# Revit family: NAU_Naughtone_Stng_Viv_4Leg1
name_source: partatom
category: Furniture
revit_build: Autodesk Revit 2018 (Build: 20170223_1515(x64)
units: mm (PartAtom-declared; Revit-internal decimal feet)

## family parameters
Always vertical = Yes
Cut with Voids When Loaded = No
OmniClass Number = 23.40.20.00
OmniClass Title = General Furniture and Specialties
Room Calculation Point = No
Shared = Yes
Work Plane-Based = No

## types (2) — shared parameters
Assembly Code = E2020200
AssetType = Movable
BIMObjectName = NAU_Naughtone_Seating_Viv_4Leg
Category = Pr_40_50_12 : Chairs, seats and benches
Color = Various
DurationUnit = year
Finish = Fabric Upholstery
IfcExportAs = IfcFurnishingElementType
IfcExportType = CHAIR
Keynote = Pr_40_50_12
MainColor = Various
ManufacturerAddress = Knaresborough Tech Park, Manse Lane, Knaresborough, HG5 8LF
ManufacturerName = Naughtone
ManufacturerURL = www.naughtone.com
Material = Fabric, Foam, Polypropylene, Steel
NBSDescription = Seating
NBSReference = 45-35-72/352
Name = Seating_Viv_4Leg_Naughtone
NominalHeight = 810 mm
ProductInformation = www.naughtone.com/products/viv/
Revision = 1
Shape = Rectangular
SustainabilityPerformance = FSC certified. FISP certified. ISO 14001
URL = www.naughtone.com
Uniclass2015Code = Pr_40_50_12
Uniclass2015Title = Chairs, seats and benches
Version = 1
WarrantyDescription = Request warranty information from naughtone
WarrantyDurationLabor = 7
WarrantyDurationParts = 7
WarrantyDurationUnit = year

## per-type parameters (varying)
| type | Description | IsVIVCHB4L | IsVIVCHBDL | Model | ModelNumber | ModelReference | NominalLength | NominalWidth | Size |
| Viv chair with 4 leg base_VIVCHB4L | Viv chair with 4 leg base | Yes | No | VIVCHB4L | VIVCHB4L | Viv chair with 4 leg base | 560 mm | 550 mm | 560 x 550 x 810 mm |
| Viv Chair Dowel Base_VIVCHBDL | Viv Chair Dowel Base | No | Yes | VIVCHBDL | VIVCHBDL | Viv Chair Dowel Base | 555 mm | 505 mm | 555 x 505 x 810 mm |

## geometry (parser evidence)
native form markers: Sweep x2
no freeform markers — native parametric forms only
